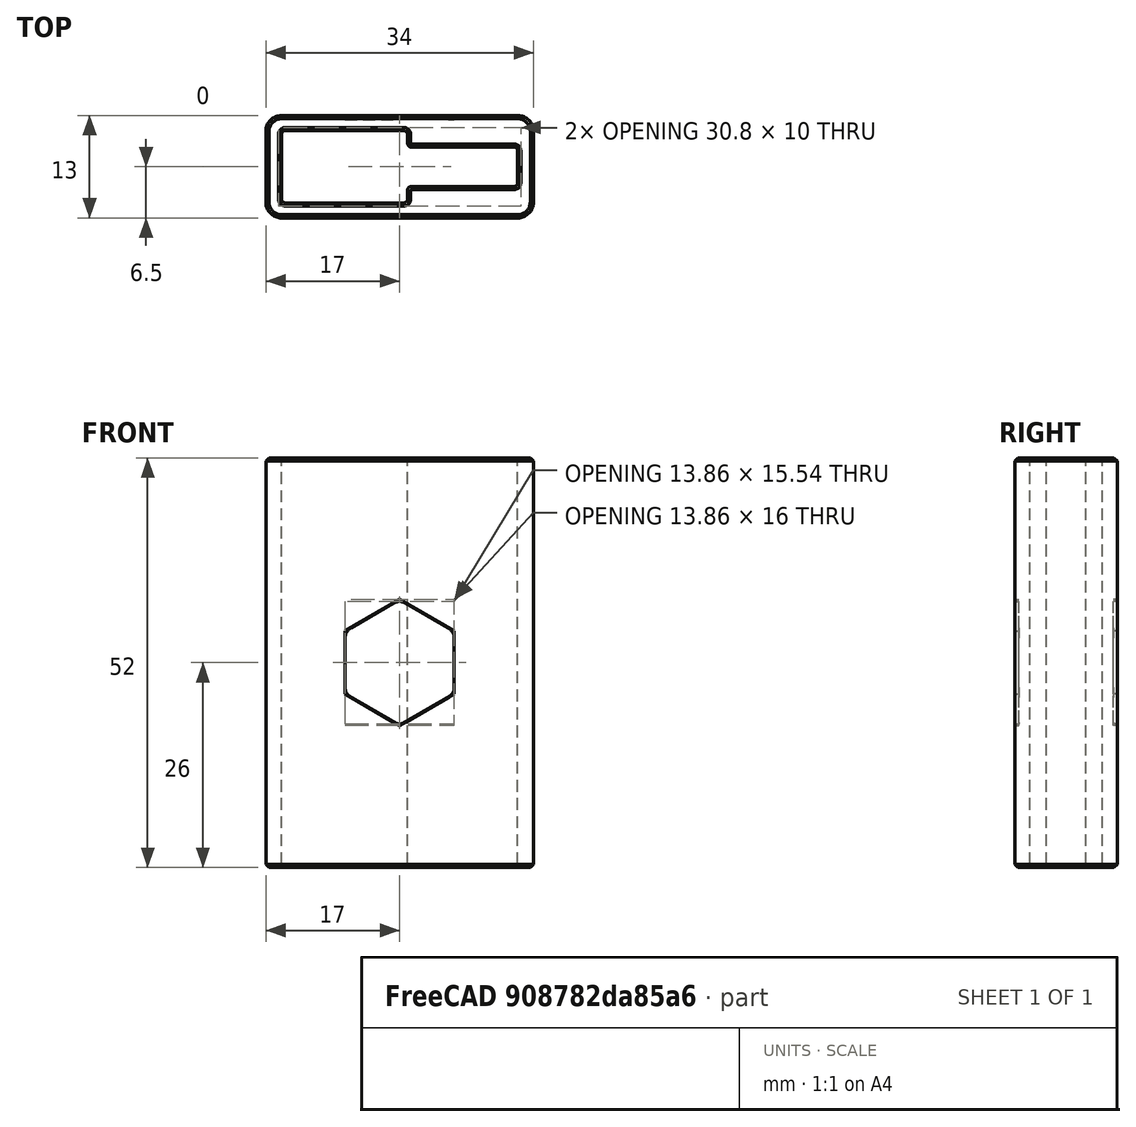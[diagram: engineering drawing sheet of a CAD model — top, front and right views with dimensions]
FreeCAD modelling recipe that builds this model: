
FCSTD DOCUMENT  (FreeCAD 0.17R13522 (Git))
Label: lidl_taco_puntas_allen
License: All rights reserved
LicenseURL: http://en.wikipedia.org/wiki/All_rights_reserved
objects: Part::Box×3, Part::Fillet×3, Mesh::Feature×1, Part::Fuse×1, Part::Cut×1, Part::Chamfer×1, PartDesign::FeatureBase×1, Sketcher::SketchObject×1, PartDesign::Pocket×1, PartDesign::Mirrored×1, PartDesign::Body×1
note: 15 computed .brp shape members not serialized (recipe doc carries the construction recipe); baked Part::Feature solids carry a one-line shape summary decoded from their .brp

FEATURE [Mesh::Feature] lidl
FEATURE [Part::Box] Box  label="Cubo"
  AttacherType = Attacher::AttachEngine3D
  Height = 60
  Length = 16
  Placement = pos=(0,-4.6,0) rot=(0,0,1;0rad)
  Width = 9.2
FEATURE [Part::Box] Box001  label="Cubo001"
  AttacherType = Attacher::AttachEngine3D
  Height = 60
  Length = 30
  Placement = pos=(0,-2.5,0) rot=(0,0,1;0rad)
  Width = 5
FEATURE [Part::Fuse] Fusion
  Base = -> Box
  Refine = true
  Tool = -> Box001
FEATURE [Part::Fillet] Fillet
  Base = -> Fusion
  Edges = 8 edges r=0.5: [Edge2,Edge4,Edge6,Edge9,Edge12,Edge16,Edge18,Edge20]
FEATURE [Part::Box] Box002  label="Cubo002"
  AttacherType = Attacher::AttachEngine3D
  Height = 52
  Length = 34
  Placement = pos=(-2,-6.5,0) rot=(0,0,1;0rad)
  Width = 13
FEATURE [Part::Cut] Cut
  Base = -> Box002
  Refine = true
  Tool = -> Fillet
FEATURE [Part::Fillet] Fillet001
  Base = -> Cut
  Edges = 4 edges r=2: [Edge1,Edge3,Edge6,Edge27]
FEATURE [Part::Chamfer] Chamfer
  Base = -> Fillet001
  Edges = 48 edges r=0.4: [Edge1,Edge4,Edge5,Edge6,Edge7,Edge8,Edge9,Edge10,Edge11,Edge12,Edge13,Edge14,Edge15,Edge16,Edge17,Edge18,Edge19,Edge20,Edge21,Edge22,Edge23,Edge24,Edge25,Edge26,Edge27,Edge28,Edge30,Edge32,Edge33,Edge34,Edge35,Edge36,Edge37,Edge38,Edge39,Edge40,Edge41,Edge42,Edge43,Edge44,Edge45,Edge46,Edge47,+5 more]
FEATURE [PartDesign::FeatureBase] BaseFeature
  BaseFeature = -> Chamfer
FEATURE [Sketcher::SketchObject] Sketch
  MapMode = 5
  Placement = pos=(0,-6.5,0) rot=(1,0,0;1.5708rad)
  Support = -> [BaseFeature]
  sketch-geometry (7):
    g0: LineSegment StartX=15 StartY=34 StartZ=0 EndX=8.0718 EndY=30 EndZ=0
    g1: LineSegment StartX=8.0718 StartY=30 StartZ=0 EndX=8.0718 EndY=22 EndZ=0
    g2: LineSegment StartX=8.0718 StartY=22 StartZ=0 EndX=15 EndY=18 EndZ=0
    g3: LineSegment StartX=15 StartY=18 StartZ=0 EndX=21.9282 EndY=22 EndZ=0
    g4: LineSegment StartX=21.9282 StartY=22 StartZ=0 EndX=21.9282 EndY=30 EndZ=0
    g5: LineSegment StartX=21.9282 StartY=30 StartZ=0 EndX=15 EndY=34 EndZ=0
    g6: Circle [constr] CenterX=15 CenterY=26 CenterZ=0 NormalX=0 NormalY=0 NormalZ=1 AngleXU=0 Radius=8
  constraints (17):
    c: Coincident(g0,g1)
    c: Coincident(g1,g2)
    c: Coincident(g2,g3)
    c: Coincident(g3,g4)
    c: Coincident(g4,g5)
    c: Coincident(g5,g0)
    c: Equal(g0, g1-g5) x5
    c: PointOnObject(g0,g6)
    c: PointOnObject(g1,g6)
    c: PointOnObject(g2,g6)
    c: PointOnObject(g3,g6)
    c: PointOnObject(g4,g6)
    c: PointOnObject(g5,g6)
    c: Vertical(g4)
    c: DistanceX(g-1,g6) = 15
    c: DistanceY(g-1,g6) = 26
    c: Radius(g6) = 8
FEATURE [PartDesign::Pocket] Pocket
  BaseFeature = -> BaseFeature
  Length = 0.5
  Length2 = 100
  Profile = -> Sketch
  Refine = true
  Type = 0
FEATURE [PartDesign::Mirrored] Mirrored
  BaseFeature = -> Pocket
  MirrorPlane = -> XZ_Plane
  Originals = -> [Pocket]
  Refine = true
FEATURE [PartDesign::Body] Body
  BaseFeature = -> Chamfer
  Group = -> [BaseFeature,Sketch,Pocket,Mirrored]
  Origin = -> Origin
  Tip = -> Mirrored
FEATURE [Part::Fillet] Fillet002
  Base = -> Mirrored
  Edges = 12 edges r=1.5: [Edge90,Edge92,Edge93,Edge95,Edge97,Edge99,Edge177,Edge179,Edge180,Edge182,Edge184,Edge186]
